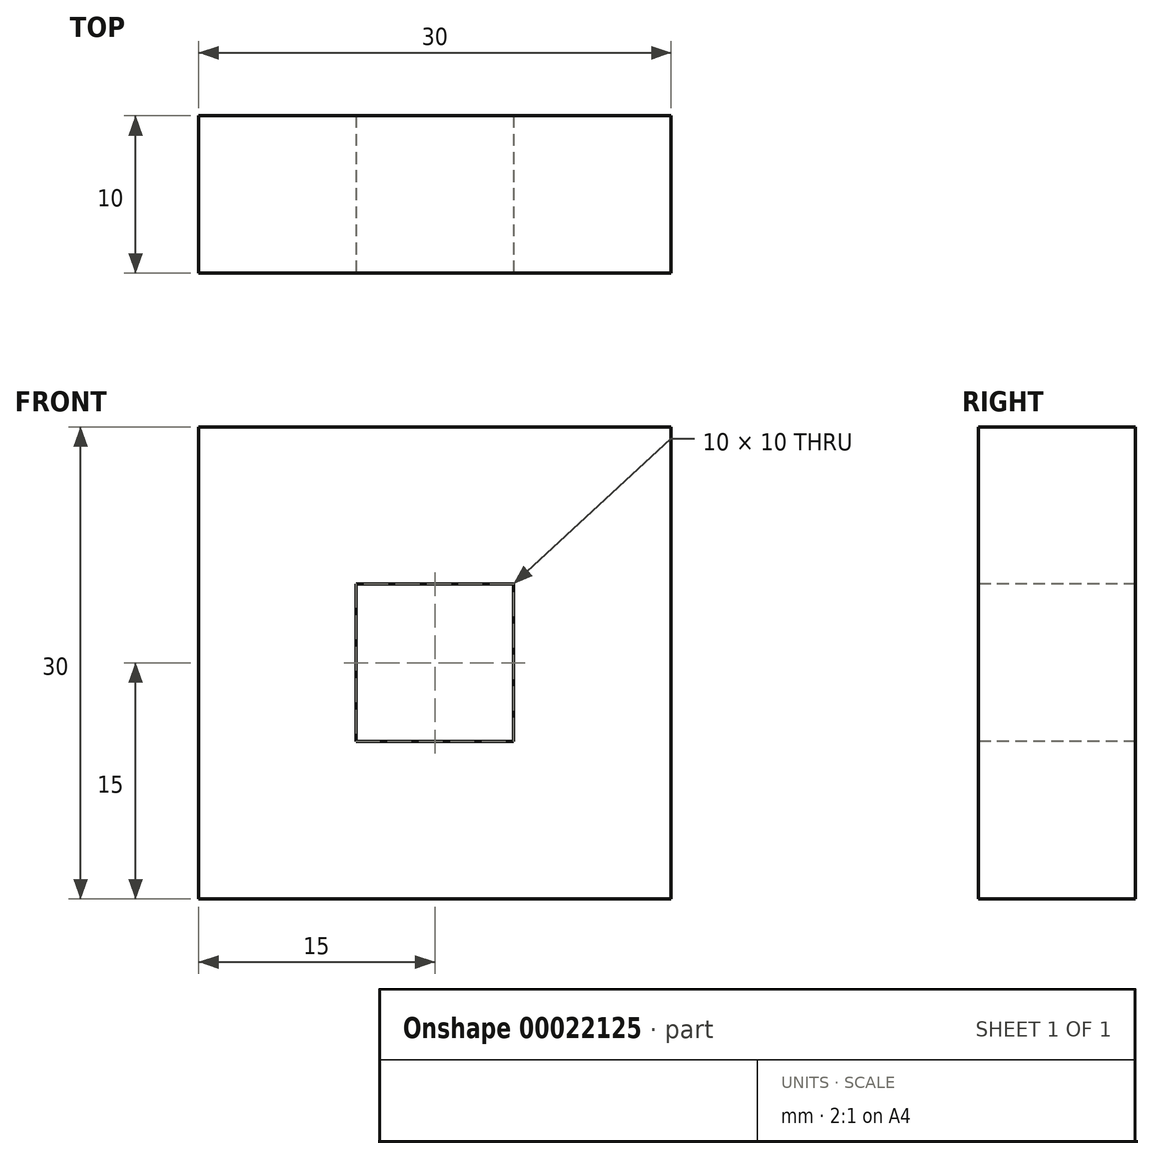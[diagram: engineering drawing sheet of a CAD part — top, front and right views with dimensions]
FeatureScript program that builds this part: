
annotation { "Feature Type Name" : "Feature", "Feature Type Description" : "" }
export const myFeature = defineFeature(function(context is Context, id is Id, definition is map)
    precondition{}
    {
        {
            var Q0;
            Q0=qCreatedBy(makeId("Front.planeOp"),FACE);
            var sketch = newSketch(context, id + "F0", { "sketchPlane" : qUnion([Q0])});
            skLineSegment(sketch, "E0.rect.bottom", {"start": v(15, -15) * mm, "end": v(-15, -15) * mm});
            skLineSegment(sketch, "E0.rect.top", {"start": v(15, 15) * mm, "end": v(-15, 15) * mm});
            skLineSegment(sketch, "E0.rect.left", {"start": v(15, -15) * mm, "end": v(15, 15) * mm});
            skLineSegment(sketch, "E0.rect.right", {"start": v(-15, -15) * mm, "end": v(-15, 15) * mm});
            skPoint(sketch, "E0.rect.middle", {"position": v(0, 0) * mm});
            skSolve(sketch);
        }
        {
            var Q0;
            Q0=makeQuery(id+"F0.imprint","IMPRINT",FACE,{"disambiguationData":[TD([[makeQuery(id+"F0.imprint","IMPRINT",EDGE,{"derivedFrom":sQuery(id+"F0.wireOp",EDGE,"E0.rect.bottom")}),-1.0]])]});
            extrude(context, id + "F1", {"entities" : qUnion([Q0]), "depth" : 10 * mm});
        }
        {
            var Q0;
            Q0=makeQuery(id+"F1.opExtrude","CAP_FACE",FACE,{"disambiguationData":[OSD([sQuery(id+"F0.wireOp",EDGE,"E0.rect.bottom"),sQuery(id+"F0.wireOp",EDGE,"E0.rect.top"),sQuery(id+"F0.wireOp",EDGE,"E0.rect.left"),sQuery(id+"F0.wireOp",EDGE,"E0.rect.right")])],"isStart":false});
            var sketch = newSketch(context, id + "F2", { "sketchPlane" : qUnion([Q0])});
            skLineSegment(sketch, "E1.rect.bottom", {"start": v(5, -5) * mm, "end": v(-5, -5) * mm});
            skLineSegment(sketch, "E1.rect.top", {"start": v(5, 5) * mm, "end": v(-5, 5) * mm});
            skLineSegment(sketch, "E1.rect.left", {"start": v(5, -5) * mm, "end": v(5, 5) * mm});
            skLineSegment(sketch, "E1.rect.right", {"start": v(-5, -5) * mm, "end": v(-5, 5) * mm});
            skPoint(sketch, "E1.rect.middle", {"position": v(0, 0) * mm});
            skSolve(sketch);
        }
        {
            var Q0;
            Q0 = qSketchRegion(id + "F2", true);
            extrude(context, id + "F3", {"entities" : qUnion([Q0]), "operationType" : NewBodyOperationType.REMOVE, "endBound" : BoundingType.THROUGH_ALL, "oppositeDirection" : true, "depth" : 25 * mm});
        }
    });
